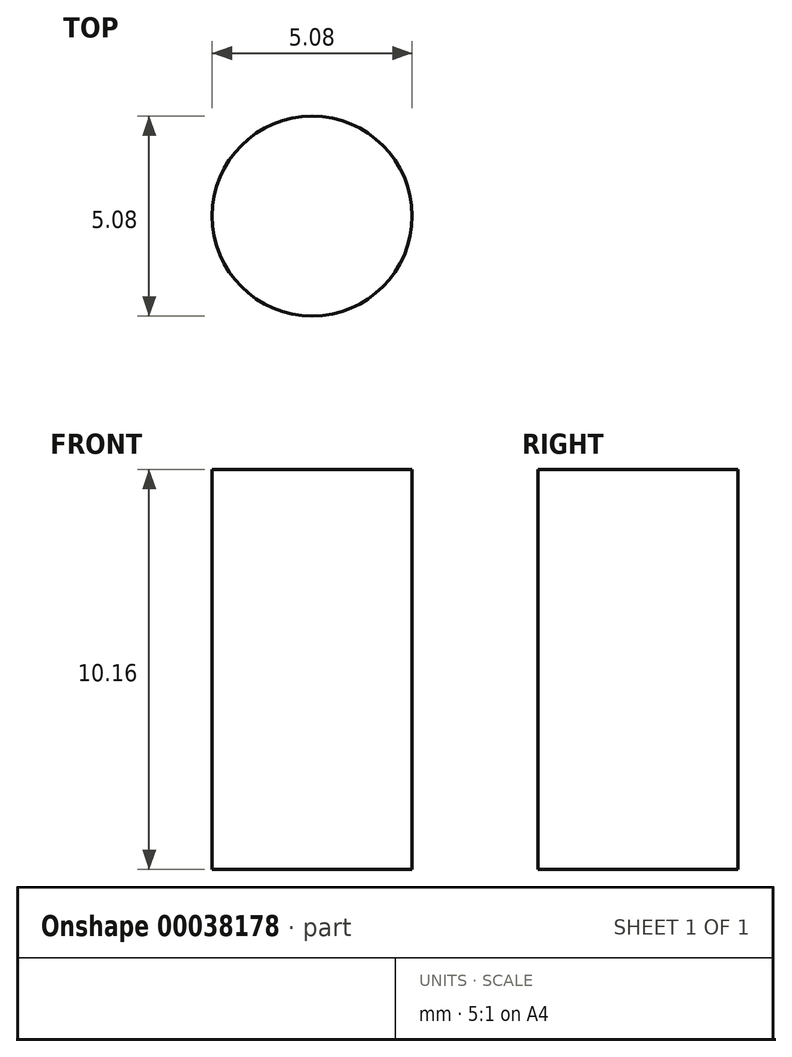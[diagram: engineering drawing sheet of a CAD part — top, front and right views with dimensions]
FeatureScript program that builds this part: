
annotation { "Feature Type Name" : "Feature", "Feature Type Description" : "" }
export const myFeature = defineFeature(function(context is Context, id is Id, definition is map)
    precondition{}
    {
        {
            var Q0;
            Q0=qCreatedBy(makeId("Top.planeOp"),FACE);
            var sketch = newSketch(context, id + "F0", { "sketchPlane" : qUnion([Q0])});
            skCircle(sketch, "E0", {"center": v(0, 0) * mm, "radius": 2.54 * mm});
            skSolve(sketch);
        }
        {
            var Q0;
            Q0 = qSketchRegion(id + "F0", true);
            extrude(context, id + "F1", {"entities" : qUnion([Q0]), "depth" : 10.16 * mm});
        }
    });
